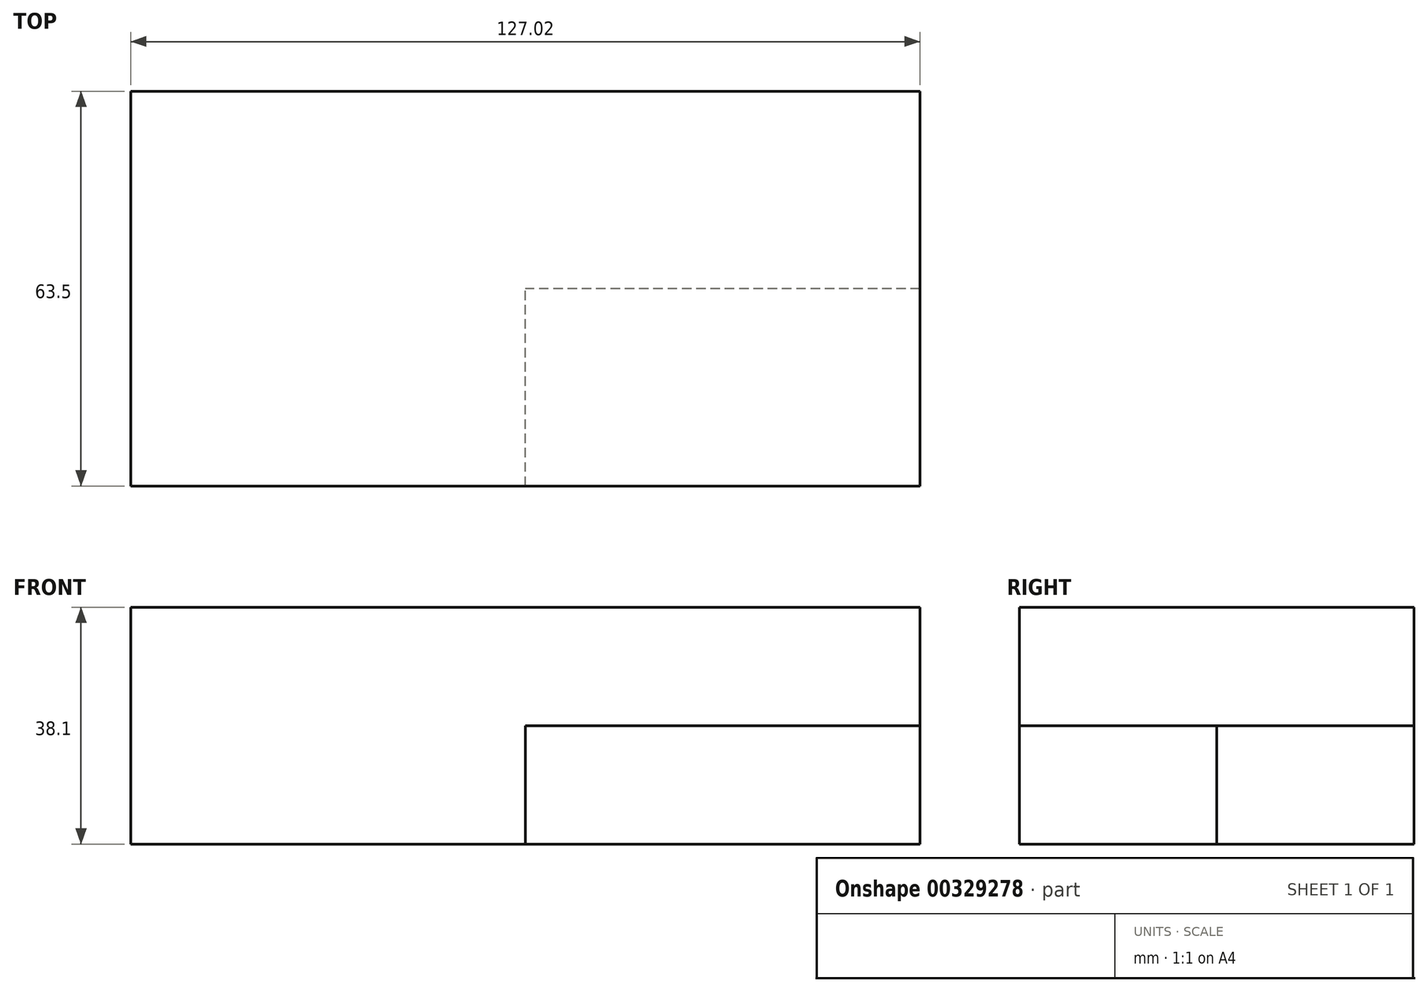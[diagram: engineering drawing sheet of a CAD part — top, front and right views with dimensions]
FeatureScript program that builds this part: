
annotation { "Feature Type Name" : "Feature", "Feature Type Description" : "" }
export const myFeature = defineFeature(function(context is Context, id is Id, definition is map)
    precondition{}
    {
        {
            var Q0;
            Q0=qCreatedBy(makeId("Front.planeOp"),FACE);
            var sketch = newSketch(context, id + "F0", { "sketchPlane" : qUnion([Q0])});
            skLineSegment(sketch, "E0", {"start": v(-61.04, 38.1) * mm, "end": v(65.96, 38.1) * mm});
            skLineSegment(sketch, "E1", {"start": v(-61.04, 38.1) * mm, "end": v(-61.04, 0) * mm});
            skLineSegment(sketch, "E2", {"start": v(-61.04, 0) * mm, "end": v(2.46, 0) * mm});
            skLineSegment(sketch, "E3", {"start": v(65.96, 38.1) * mm, "end": v(65.96, 19.05) * mm});
            skLineSegment(sketch, "E4", {"start": v(2.46, 0) * mm, "end": v(65.98, 0) * mm});
            skLineSegment(sketch, "E5", {"start": v(65.98, 0) * mm, "end": v(65.96, 19.05) * mm});
            skSolve(sketch);
        }
        {
            var Q0;
            Q0=makeQuery(id+"F0.imprint","IMPRINT",FACE,{"disambiguationData":[TD([[makeQuery(id+"F0.imprint","IMPRINT",EDGE,{"derivedFrom":sQuery(id+"F0.wireOp",EDGE,"E0")}),-1.0]])]});
            extrude(context, id + "F1", {"entities" : qUnion([Q0]), "depth" : 63.5 * mm});
        }
        {
            var Q0;
            Q0=qCreatedBy(makeId("Front.planeOp"),FACE);
            var sketch = newSketch(context, id + "F2", { "sketchPlane" : qUnion([Q0])});
            skLineSegment(sketch, "E6", {"start": v(65.98, 0) * mm, "end": v(2.48, 0) * mm});
            skLineSegment(sketch, "E7", {"start": v(65.98, 0) * mm, "end": v(65.98, 19.06) * mm});
            skLineSegment(sketch, "E8", {"start": v(65.98, 19.06) * mm, "end": v(2.49, 19.06) * mm});
            skLineSegment(sketch, "E9", {"start": v(2.49, 19.06) * mm, "end": v(2.48, 0) * mm});
            skSolve(sketch);
        }
        {
            var Q0;
            Q0 = qSketchRegion(id + "F2", true);
            extrude(context, id + "F3", {"entities" : qUnion([Q0]), "operationType" : NewBodyOperationType.REMOVE, "depth" : 72.14 * mm});
        }
        {
            var Q0;
            Q0 = qSketchRegion(id + "F2", true);
            extrude(context, id + "F4", {"entities" : qUnion([Q0]), "operationType" : NewBodyOperationType.ADD, "depth" : 31.75 * mm});
        }
    });
